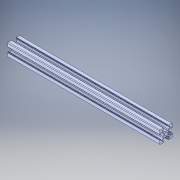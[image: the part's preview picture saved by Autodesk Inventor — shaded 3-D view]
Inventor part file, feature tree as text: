
AUTODESK INVENTOR PART (.ipt)
format: ipt  version: 2018 (Build 220112000, 112)  size: 371,200 bytes
history: native  units: in
note: dims shown in document units (in); Inventor stores cm internally (conversion verified against a paired STEP export)
features: extrude x1, sketch x1, projected_geometry x1, fillet x1
ambient origin geometry x8: Origin, YZ Plane, XZ Plane, XY Plane, X Axis, Y Axis, Z Axis, Center Point
bodies: Solid1 (feature_tree)
feature tree (4):
  extrude  "Extrusion2"  [1 undecoded]
  sketch  "Sketch3"  dims[d2=5.5118in d3=0.0in]
  projected_geometry  "Projected Loop2"
  fillet  "Fillet5"  [1 undecoded]
note: 2 required parameter values undecoded (feature->parameter linkage not recoverable at this tier; creation-order binding heuristic only, values carry confidence <= 0.55)
